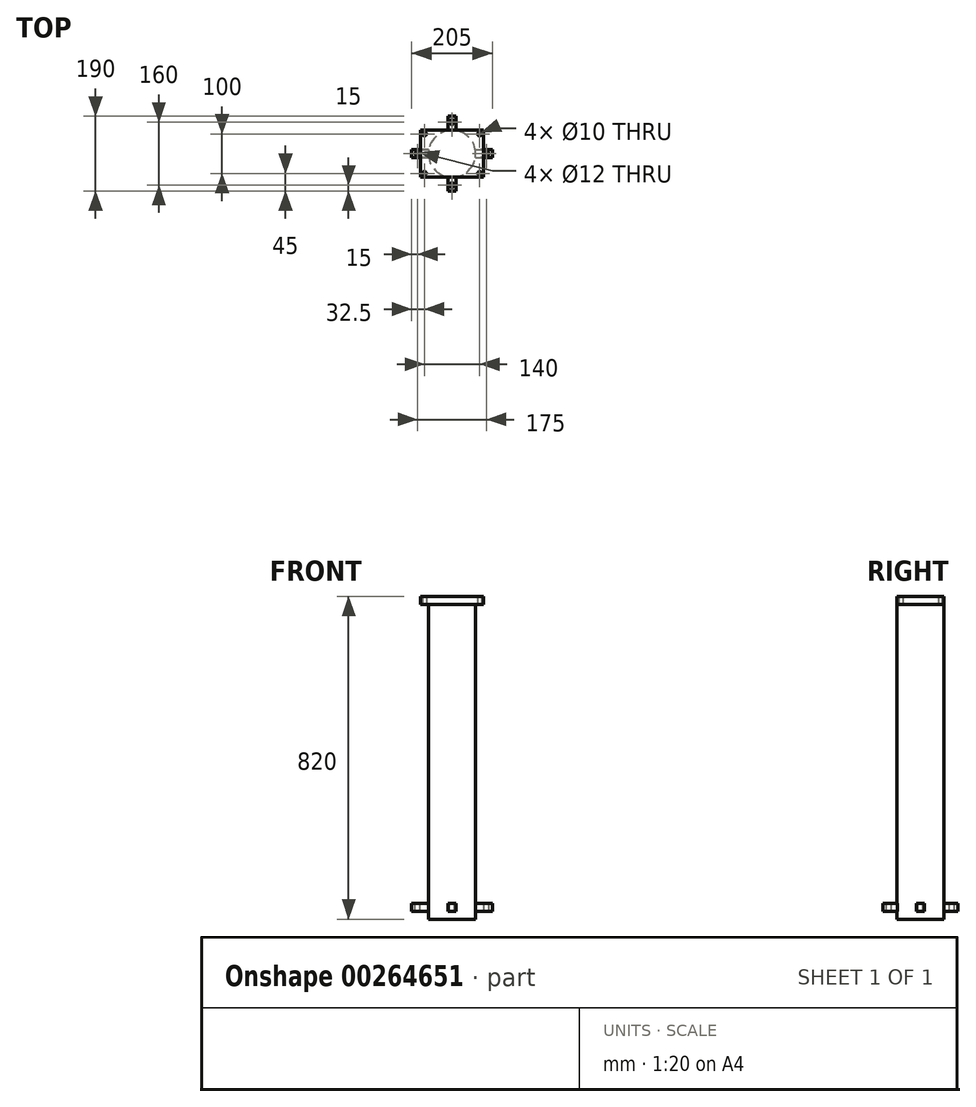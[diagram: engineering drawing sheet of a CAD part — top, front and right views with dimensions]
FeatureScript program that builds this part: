
annotation { "Feature Type Name" : "Feature", "Feature Type Description" : "" }
export const myFeature = defineFeature(function(context is Context, id is Id, definition is map)
    precondition{}
    {
        {
            var Q0;
            Q0=qCreatedBy(makeId("Top.planeOp"),FACE);
            var sketch = newSketch(context, id + "F0", { "sketchPlane" : qUnion([Q0])});
            skCircle(sketch, "E0", {"center": v(0, 0) * mm, "radius": 60 * mm});
            skLineSegment(sketch, "E1", {"start": v(-10, 59.16) * mm, "end": v(-10, 95) * mm});
            skLineSegment(sketch, "E2", {"start": v(-10, 95) * mm, "end": v(10, 95) * mm});
            skLineSegment(sketch, "E3", {"start": v(10, 95) * mm, "end": v(10, 59.16) * mm});
            skLineSegment(sketch, "E4", {"start": v(59.16, 10) * mm, "end": v(102.5, 10) * mm});
            skLineSegment(sketch, "E5", {"start": v(102.5, 10) * mm, "end": v(102.5, -10) * mm});
            skLineSegment(sketch, "E6", {"start": v(102.5, -10) * mm, "end": v(59.16, -10) * mm});
            skLineSegment(sketch, "E7", {"start": v(10, -59.16) * mm, "end": v(10, -95) * mm});
            skLineSegment(sketch, "E8", {"start": v(10, -95) * mm, "end": v(-10, -95) * mm});
            skLineSegment(sketch, "E9", {"start": v(-10, -95) * mm, "end": v(-10, -59.16) * mm});
            skLineSegment(sketch, "E10", {"start": v(-59.16, -10) * mm, "end": v(-102.5, -10) * mm});
            skLineSegment(sketch, "E11", {"start": v(-102.5, -10) * mm, "end": v(-102.5, 10) * mm});
            skLineSegment(sketch, "E12", {"start": v(-102.5, 10) * mm, "end": v(-59.16, 10) * mm});
            skLineSegment(sketch, "E13.bottom", {"start": v(-80, 60) * mm, "end": v(80, 60) * mm});
            skLineSegment(sketch, "E13.top", {"start": v(-80, -60) * mm, "end": v(80, -60) * mm});
            skLineSegment(sketch, "E13.left", {"start": v(-80, 60) * mm, "end": v(-80, -60) * mm});
            skLineSegment(sketch, "E13.right", {"start": v(80, 60) * mm, "end": v(80, -60) * mm});
            skCircle(sketch, "E14", {"center": v(0, 80) * mm, "radius": 6 * mm});
            skCircle(sketch, "E15", {"center": v(87.5, 0) * mm, "radius": 6 * mm});
            skCircle(sketch, "E16", {"center": v(-87.5, 0) * mm, "radius": 6 * mm});
            skCircle(sketch, "E17", {"center": v(0, -80) * mm, "radius": 6 * mm});
            skLineSegment(sketch, "E18.0", {"start": v(-70, 50) * mm, "end": v(70, 50) * mm, "construction": true});
            skLineSegment(sketch, "E18.1", {"start": v(-70, 50) * mm, "end": v(-70, -50) * mm, "construction": true});
            skLineSegment(sketch, "E18.2", {"start": v(-70, -50) * mm, "end": v(70, -50) * mm, "construction": true});
            skLineSegment(sketch, "E18.3", {"start": v(70, 50) * mm, "end": v(70, -50) * mm, "construction": true});
            skCircle(sketch, "E19", {"center": v(-70, -50) * mm, "radius": 5 * mm});
            skCircle(sketch, "E20", {"center": v(-70, 50) * mm, "radius": 5 * mm});
            skCircle(sketch, "E21", {"center": v(70, 50) * mm, "radius": 5 * mm});
            skCircle(sketch, "E22", {"center": v(70, -50) * mm, "radius": 5 * mm});
            skSolve(sketch);
        }
        {
            var Q0;
            Q0=makeQuery(id+"F0.imprint","IMPRINT",FACE,{"disambiguationData":[TD([[makeQuery(id+"F0.imprint","IMPRINT",EDGE,{"derivedFrom":sQuery(id+"F0.wireOp",EDGE,"E20")}),-1.0]])]});
            var Q1;
            {var subQ0=sQuery(id+"F0.wireOp",EDGE,"E0");var subQ4=makeQuery(id+"F0.imprint","INTERSECT",VERTEX,{"derivedFrom":[subQ0,sQuery(id+"F0.wireOp",EDGE,"E3")]});Q1=makeQuery(id+"F0.imprint","IMPRINT",FACE,{"disambiguationData":[TD([[makeQuery(id+"F0.imprint","IMPRINT",EDGE,{"disambiguationData":[TD([[subQ4,1.0]])],"derivedFrom":subQ0}),1.0]])]});}
            var Q2;
            Q2=makeQuery(id+"F0.imprint","IMPRINT",FACE,{"disambiguationData":[TD([[makeQuery(id+"F0.imprint","IMPRINT",EDGE,{"derivedFrom":sQuery(id+"F0.wireOp",EDGE,"E21")}),-1.0]])]});
            var Q3;
            {var subQ0=sQuery(id+"F0.wireOp",EDGE,"E4");var subQ1=sQuery(id+"F0.wireOp",EDGE,"E0");var subQ2=makeQuery(id+"F0.imprint","INTERSECT",VERTEX,{"derivedFrom":[subQ1,subQ0]});Q3=makeQuery(id+"F0.imprint","IMPRINT",FACE,{"disambiguationData":[TD([[makeQuery(id+"F0.imprint","IMPRINT",EDGE,{"disambiguationData":[TD([[subQ2,1.0]])],"derivedFrom":subQ1}),-1.0]])]});}
            var Q4;
            Q4=makeQuery(id+"F0.imprint","IMPRINT",FACE,{"disambiguationData":[TD([[makeQuery(id+"F0.imprint","IMPRINT",EDGE,{"derivedFrom":sQuery(id+"F0.wireOp",EDGE,"E22")}),-1.0]])]});
            var Q5;
            {var subQ0=sQuery(id+"F0.wireOp",EDGE,"E10");var subQ1=sQuery(id+"F0.wireOp",EDGE,"E0");var subQ2=makeQuery(id+"F0.imprint","INTERSECT",VERTEX,{"derivedFrom":[subQ1,subQ0]});Q5=makeQuery(id+"F0.imprint","IMPRINT",FACE,{"disambiguationData":[TD([[makeQuery(id+"F0.imprint","IMPRINT",EDGE,{"disambiguationData":[TD([[subQ2,1.0]])],"derivedFrom":subQ1}),-1.0]])]});}
            var Q6;
            Q6=makeQuery(id+"F0.imprint","IMPRINT",FACE,{"disambiguationData":[TD([[makeQuery(id+"F0.imprint","IMPRINT",EDGE,{"derivedFrom":sQuery(id+"F0.wireOp",EDGE,"E19")}),-1.0]])]});
            var Q7;
            {var subQ0=sQuery(id+"F0.wireOp",EDGE,"E16");var subQ1=sQuery(id+"F0.wireOp",EDGE,"E13.left");var subQ2=makeQuery(id+"F0.imprint","INTERSECT",VERTEX,{"disambiguationData":[OD(0.0)],"derivedFrom":[subQ1,subQ0]});Q7=makeQuery(id+"F0.imprint","IMPRINT",FACE,{"disambiguationData":[TD([[makeQuery(id+"F0.imprint","IMPRINT",EDGE,{"disambiguationData":[TD([[subQ2,-1.0]])],"derivedFrom":subQ1}),1.0]])]});}
            var Q8;
            {var subQ0=sQuery(id+"F0.wireOp",EDGE,"E15");var subQ1=sQuery(id+"F0.wireOp",EDGE,"E13.right");var subQ2=makeQuery(id+"F0.imprint","INTERSECT",VERTEX,{"disambiguationData":[OD(0.0)],"derivedFrom":[subQ1,subQ0]});Q8=makeQuery(id+"F0.imprint","IMPRINT",FACE,{"disambiguationData":[TD([[makeQuery(id+"F0.imprint","IMPRINT",EDGE,{"disambiguationData":[TD([[subQ2,-1.0]])],"derivedFrom":subQ1}),-1.0]])]});}
            var Q9;
            {var subQ0=sQuery(id+"F0.wireOp",EDGE,"E9");var subQ1=sQuery(id+"F0.wireOp",EDGE,"E0");var subQ2=makeQuery(id+"F0.imprint","INTERSECT",VERTEX,{"derivedFrom":[subQ1,subQ0]});Q9=makeQuery(id+"F0.imprint","IMPRINT",FACE,{"disambiguationData":[TD([[makeQuery(id+"F0.imprint","IMPRINT",EDGE,{"disambiguationData":[TD([[subQ2,-1.0]])],"derivedFrom":subQ1}),-1.0]])]});}
            var Q10;
            {var subQ0=sQuery(id+"F0.wireOp",EDGE,"E7");var subQ1=sQuery(id+"F0.wireOp",EDGE,"E0");var subQ2=makeQuery(id+"F0.imprint","INTERSECT",VERTEX,{"derivedFrom":[subQ1,subQ0]});Q10=makeQuery(id+"F0.imprint","IMPRINT",FACE,{"disambiguationData":[TD([[makeQuery(id+"F0.imprint","IMPRINT",EDGE,{"disambiguationData":[TD([[subQ2,1.0]])],"derivedFrom":subQ1}),-1.0]])]});}
            var Q11;
            {var subQ0=sQuery(id+"F0.wireOp",EDGE,"E1");var subQ1=sQuery(id+"F0.wireOp",EDGE,"E0");var subQ2=makeQuery(id+"F0.imprint","INTERSECT",VERTEX,{"derivedFrom":[subQ1,subQ0]});Q11=makeQuery(id+"F0.imprint","IMPRINT",FACE,{"disambiguationData":[TD([[makeQuery(id+"F0.imprint","IMPRINT",EDGE,{"disambiguationData":[TD([[subQ2,1.0]])],"derivedFrom":subQ1}),-1.0]])]});}
            var Q12;
            {var subQ0=sQuery(id+"F0.wireOp",EDGE,"E3");var subQ1=sQuery(id+"F0.wireOp",EDGE,"E0");var subQ2=makeQuery(id+"F0.imprint","INTERSECT",VERTEX,{"derivedFrom":[subQ1,subQ0]});Q12=makeQuery(id+"F0.imprint","IMPRINT",FACE,{"disambiguationData":[TD([[makeQuery(id+"F0.imprint","IMPRINT",EDGE,{"disambiguationData":[TD([[subQ2,-1.0]])],"derivedFrom":subQ1}),-1.0]])]});}
            extrude(context, id + "F1", {"entities" : qUnion([Q0, Q1, Q2, Q3, Q4, Q5, Q6, Q7, Q8, Q9, Q10, Q11, Q12]), "depth" : 20 * mm});
        }
        {
            var Q0;
            {var subQ0=sQuery(id+"F0.wireOp",EDGE,"E0");var subQ4=makeQuery(id+"F0.imprint","INTERSECT",VERTEX,{"derivedFrom":[subQ0,sQuery(id+"F0.wireOp",EDGE,"E3")]});Q0=makeQuery(id+"F0.imprint","IMPRINT",FACE,{"disambiguationData":[TD([[makeQuery(id+"F0.imprint","IMPRINT",EDGE,{"disambiguationData":[TD([[subQ4,1.0]])],"derivedFrom":subQ0}),1.0]])]});}
            extrude(context, id + "F2", {"entities" : qUnion([Q0]), "operationType" : NewBodyOperationType.ADD, "oppositeDirection" : true, "depth" : 800 * mm});
        }
        {
            var Q0;
            Q0=qCreatedBy(makeId("Front.planeOp"),FACE);
            var sketch = newSketch(context, id + "F3", { "sketchPlane" : qUnion([Q0])});
            skLineSegment(sketch, "E23", {"start": v(0, -760) * mm, "end": v(102.5, -760) * mm});
            skLineSegment(sketch, "E24", {"start": v(102.5, -760) * mm, "end": v(102.5, -780) * mm});
            skLineSegment(sketch, "E25", {"start": v(102.5, -780) * mm, "end": v(-102.5, -780) * mm});
            skLineSegment(sketch, "E26", {"start": v(-102.5, -780) * mm, "end": v(-102.5, -760) * mm});
            skLineSegment(sketch, "E27", {"start": v(-102.5, -760) * mm, "end": v(0, -760) * mm});
            skLineSegment(sketch, "E28.0.0", {"start": v(60, -800) * mm, "end": v(-60, -800) * mm});
            skSolve(sketch);
        }
        {
            var Q0;
            Q0=qCreatedBy(makeId("Right.planeOp"),FACE);
            var sketch = newSketch(context, id + "F4", { "sketchPlane" : qUnion([Q0])});
            skLineSegment(sketch, "E29", {"start": v(0, -760) * mm, "end": v(-95, -760) * mm});
            skLineSegment(sketch, "E30", {"start": v(-95, -760) * mm, "end": v(-95, -780) * mm});
            skLineSegment(sketch, "E31", {"start": v(-95, -780) * mm, "end": v(95, -780) * mm});
            skLineSegment(sketch, "E32", {"start": v(95, -780) * mm, "end": v(95, -760) * mm});
            skLineSegment(sketch, "E33", {"start": v(95, -760) * mm, "end": v(0, -760) * mm});
            skLineSegment(sketch, "E34.0.0", {"start": v(60, -800) * mm, "end": v(-60, -800) * mm});
            skSolve(sketch);
        }
        {
            var Q0;
            Q0=makeQuery(id+"F4.imprint","IMPRINT",FACE,{"disambiguationData":[TD([[makeQuery(id+"F4.imprint","IMPRINT",EDGE,{"derivedFrom":sQuery(id+"F4.wireOp",EDGE,"E29")}),1.0]])]});
            extrude(context, id + "F5", {"entities" : qUnion([Q0]), "operationType" : NewBodyOperationType.ADD, "endBound" : BoundingType.SYMMETRIC, "depth" : 20 * mm});
        }
        {
            var Q0;
            Q0=makeQuery(id+"F3.imprint","IMPRINT",FACE,{"disambiguationData":[TD([[makeQuery(id+"F3.imprint","IMPRINT",EDGE,{"derivedFrom":sQuery(id+"F3.wireOp",EDGE,"E23")}),-1.0]])]});
            extrude(context, id + "F6", {"entities" : qUnion([Q0]), "operationType" : NewBodyOperationType.ADD, "endBound" : BoundingType.SYMMETRIC, "depth" : 20 * mm});
        }
        {
            var Q0;
            Q0=makeQuery(id+"F0.imprint","IMPRINT",FACE,{"disambiguationData":[TD([[makeQuery(id+"F0.imprint","IMPRINT",EDGE,{"derivedFrom":sQuery(id+"F0.wireOp",EDGE,"E14")}),1.0]])]});
            var Q1;
            Q1=makeQuery(id+"F0.imprint","IMPRINT",FACE,{"disambiguationData":[TD([[makeQuery(id+"F0.imprint","IMPRINT",EDGE,{"derivedFrom":sQuery(id+"F0.wireOp",EDGE,"E17")}),1.0]])]});
            var Q2;
            Q2=makeQuery(id+"F0.imprint","IMPRINT",FACE,{"disambiguationData":[TD([[makeQuery(id+"F0.imprint","IMPRINT",EDGE,{"derivedFrom":sQuery(id+"F0.wireOp",EDGE,"E15")}),1.0]])]});
            var Q3;
            Q3=makeQuery(id+"F0.imprint","IMPRINT",FACE,{"disambiguationData":[TD([[makeQuery(id+"F0.imprint","IMPRINT",EDGE,{"derivedFrom":sQuery(id+"F0.wireOp",EDGE,"E16")}),1.0]])]});
            extrude(context, id + "F7", {"entities" : qUnion([Q0, Q1, Q2, Q3]), "operationType" : NewBodyOperationType.REMOVE, "oppositeDirection" : true, "depth" : 956 * mm});
        }
    });
